# Revit family: BIMLIB_ПриточнаяУстановка_SwiftEC_SHUFT
name_source: partatom
category: Оборудование
revit_build: Autodesk Revit 2017 (Build: 20170118_1100(x64)
units: mm (PartAtom-declared; Revit-internal decimal feet)

## family parameters
Всегда вертикально = Да
На основе рабочей плоскости = Нет
Общий = Нет
При загрузке вырезать с полостями = Нет
Размер круглого соединителя = Использовать диаметр
Тип детали = Нормальный
Точка расчета площади = Нет

## types (2) — shared parameters
ADSK_URL документации изделия = http://www.shuft.ru
ADSK_URL страницы изделия = http://www.shuft.ru
ADSK_Версия Revit = 2017
ADSK_Версия семейства = v.1
ADSK_Единица измерения = шт.
ADSK_Завод-изготовитель = ООО «Завод ВКО» марка SHUFT
ADSK_Классификация нагрузок = Прочее
ADSK_Количество фаз = 1
ADSK_Коэффициент мощности = 1
ADSK_Материал = BIMLIB_Сталь_SHUFT
ADSK_Напряжение = 220 В
ADSK_Размер_Высота = 325 мм
ADSK_Размер_Длина = 810 мм
ADSK_Размер_Ширина = 380 мм
BL_BIM library = https://bimlib.pro
D = 160 мм
URL = http://www.shuft.ru
Высота коннекторов = 118 мм
Изготовитель = ООО «Завод ВКО» марка SHUFT
Описание = Приточная установка SWIFT предназначена для создания энергоэффективной системы вентиляции в квартире, с возможностью зонального регулирования и построения VAV-системы

## per-type parameters (varying)
| type | ADSK_Масса | ADSK_Масса_Текст | ADSK_Наименование | ADSK_Номинальная мощность | ADSK_Полная мощность | SH_Мощность вентилятора |
| Swift 500 EC | 25 | 25 | Приточная вентиляционная установка Swift 500 EC | 4200 Вт | 4200 В·А | 170 Вт |
| Swift 700 EC | 26 | 26 | Приточная вентиляционная установка Swift 700 EC | 6000 Вт | 6000 В·А | 190 Вт |

note: column(s) folded — value = type name in every type: ADSK_Код изделия, ADSK_Марка
